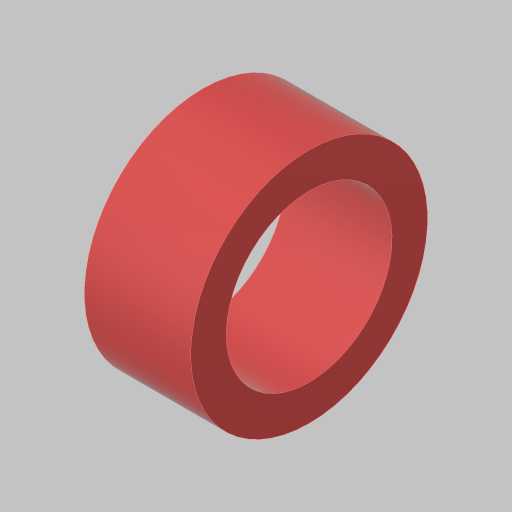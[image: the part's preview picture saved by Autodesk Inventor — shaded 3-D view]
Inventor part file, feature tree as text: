
AUTODESK INVENTOR PART (.ipt)
format: ipt  version: 2023.5 (Build 275446000, 446)  size: 107,520 bytes
history: native  units: in
note: dims shown in document units (in); Inventor stores cm internally (conversion verified against a paired STEP export)
features: extrude x1, sketch x1
ambient origin geometry x8: Origin, YZ Plane, XZ Plane, XY Plane, X Axis, Y Axis, Z Axis, Center Point
bodies: Solid1 (feature_tree)
feature tree (2):
  extrude  "Extrusion1"  Depth=0.375in
  sketch  "Sketch1"  dims[d0=0.585in d1=0.125in d2=0.375in d3=0.0in]
